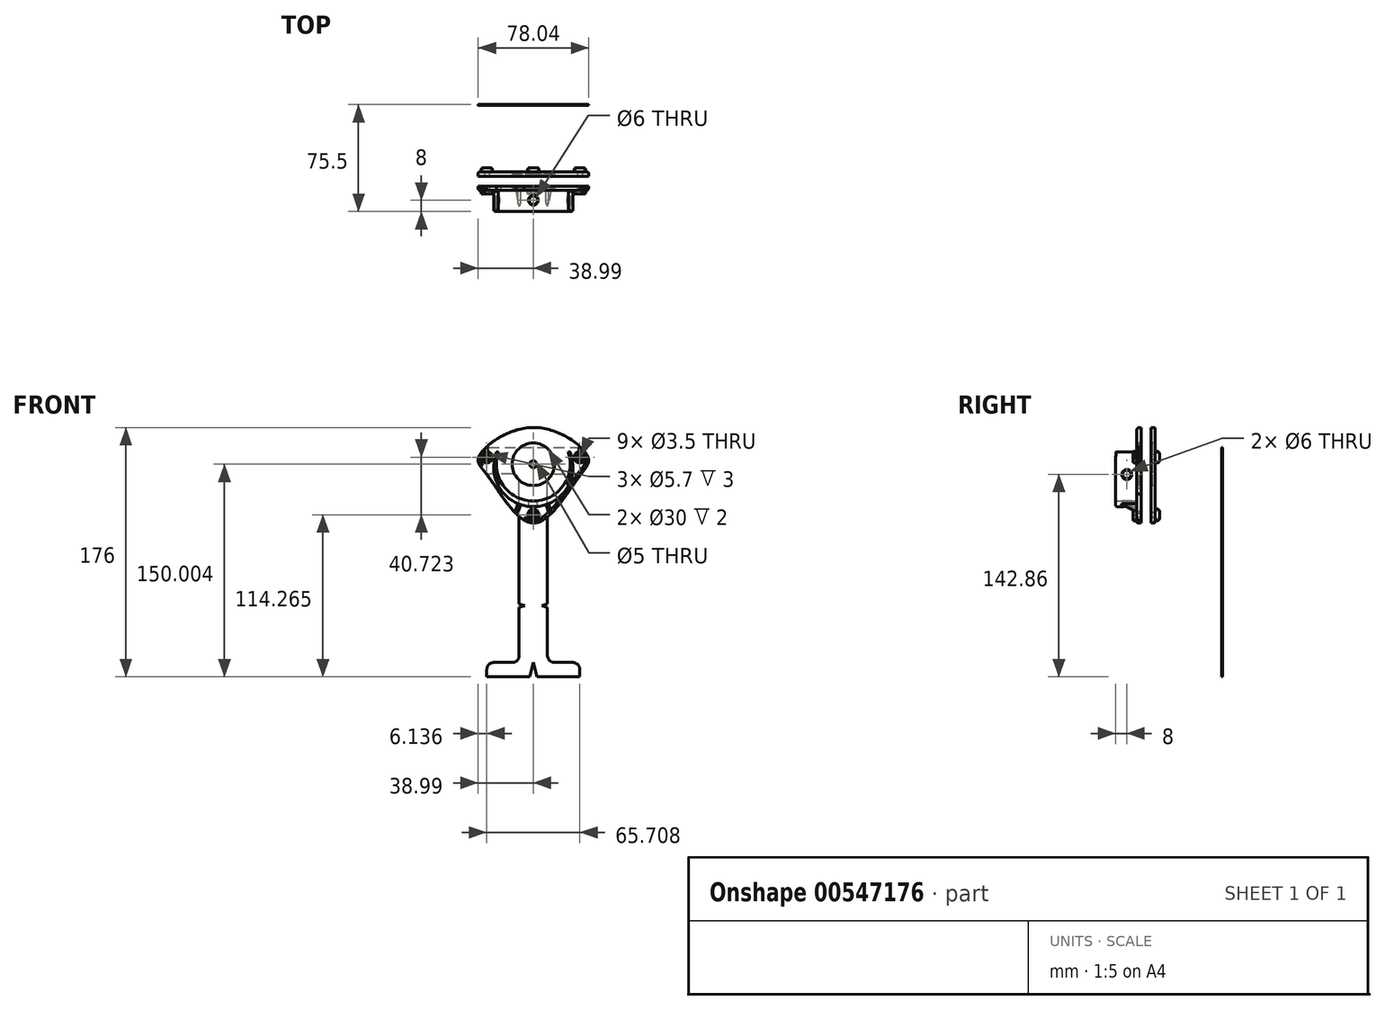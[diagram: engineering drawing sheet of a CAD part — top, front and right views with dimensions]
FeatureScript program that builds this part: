
annotation { "Feature Type Name" : "Feature", "Feature Type Description" : "" }
export const myFeature = defineFeature(function(context is Context, id is Id, definition is map)
    precondition{}
    {
        {
            var Q0;
            Q0=qCreatedBy(makeId("Front.planeOp"),FACE);
            var sketch = newSketch(context, id + "F0", { "sketchPlane" : qUnion([Q0])});
            skCircle(sketch, "E0", {"center": v(0, -2.86) * mm, "radius": 28 * mm});
            skCircle(sketch, "E1", {"center": v(0, -36.6) * mm, "radius": 1.75 * mm});
            skCircle(sketch, "E2", {"center": v(-32.85, 4.13) * mm, "radius": 1.75 * mm});
            skCircle(sketch, "E3", {"center": v(32.85, 4.13) * mm, "radius": 1.75 * mm});
            skCircle(sketch, "E4", {"center": v(0, -0.86) * mm, "radius": 26 * mm});
            skPoint(sketch, "E5", {"position": v(-38.6, 4.13) * mm});
            skPoint(sketch, "E6", {"position": v(38.6, 4.13) * mm});
            skPoint(sketch, "E7", {"position": v(0, -42.33) * mm});
            skLineSegment(sketch, "E8", {"start": v(-38.6, 4.13) * mm, "end": v(-32.85, 4.13) * mm, "construction": true});
            skLineSegment(sketch, "E9", {"start": v(-32.85, 4.13) * mm, "end": v(-27.11, 4.13) * mm, "construction": true});
            skLineSegment(sketch, "E10", {"start": v(27.11, 4.13) * mm, "end": v(32.85, 4.13) * mm, "construction": true});
            skLineSegment(sketch, "E11", {"start": v(38.6, 4.13) * mm, "end": v(32.85, 4.13) * mm, "construction": true});
            skLineSegment(sketch, "E12", {"start": v(0, -36.6) * mm, "end": v(0, -30.86) * mm, "construction": true});
            skLineSegment(sketch, "E13", {"start": v(0, -42.33) * mm, "end": v(0, -36.6) * mm, "construction": true});
            skLineSegment(sketch, "E14", {"start": v(-38.6, 0) * mm, "end": v(-38.6, 4.13) * mm, "construction": true});
            skLineSegment(sketch, "E15", {"start": v(38.6, 0) * mm, "end": v(38.6, 4.13) * mm, "construction": true});
            skPoint(sketch, "E16", {"position": v(0, 25.14) * mm});
            skFitSpline(sketch, "E17", {"points": [v(0, 25.14) * mm, v(-38.6, 4.13) * mm, v(-32.08, -9.06) * mm, v(0, -42.33) * mm, v(31.91, -10.16) * mm, v(38.6, 4.13) * mm, v(0, 25.14) * mm]});
            skLineSegment(sketch, "E18", {"start": v(-27.75, -6.56) * mm, "end": v(-32.08, -9.06) * mm, "construction": true});
            skLineSegment(sketch, "E19", {"start": v(27.58, -7.66) * mm, "end": v(31.91, -10.16) * mm, "construction": true});
            skLineSegment(sketch, "E20", {"start": v(-55.5, 8) * mm, "end": v(54.89, 8) * mm, "construction": true});
            skLineSegment(sketch, "E21", {"start": v(-25.8, 8) * mm, "end": v(-24.45, 8) * mm});
            skLineSegment(sketch, "E22", {"start": v(24.45, 8) * mm, "end": v(25.8, 8) * mm});
            skCircle(sketch, "E23", {"center": v(0, -0.86) * mm, "radius": 15 * mm});
            skCircle(sketch, "E24", {"center": v(0, -0.86) * mm, "radius": 2.5 * mm});
            skSolve(sketch);
        }
        {
            var Q0;
            Q0=makeQuery(id+"F0.imprint","IMPRINT",FACE,{"disambiguationData":[TD([[makeQuery(id+"F0.imprint","IMPRINT",EDGE,{"derivedFrom":sQuery(id+"F0.wireOp",EDGE,"E1")}),-1.0]])]});
            var Q1;
            {var subQ0=sQuery(id+"F0.wireOp",EDGE,"E21");Q1=makeQuery(id+"F0.imprint","IMPRINT",FACE,{"disambiguationData":[TD([[makeQuery(id+"F0.imprint","IMPRINT",EDGE,{"derivedFrom":subQ0}),-1.0]])]});}
            var Q2;
            {var subQ0=sQuery(id+"F0.wireOp",EDGE,"E4");var subQ4=makeQuery(id+"F0.imprint","INTERSECT",VERTEX,{"derivedFrom":[subQ0,sQuery(id+"F0.wireOp",EDGE,"E21")]});Q2=makeQuery(id+"F0.imprint","IMPRINT",FACE,{"disambiguationData":[TD([[makeQuery(id+"F0.imprint","IMPRINT",EDGE,{"disambiguationData":[TD([[subQ4,1.0]])],"derivedFrom":subQ0}),1.0]])]});}
            var Q3;
            {var subQ0=sQuery(id+"F0.wireOp",EDGE,"E21");Q3=makeQuery(id+"F0.imprint","IMPRINT",FACE,{"disambiguationData":[TD([[makeQuery(id+"F0.imprint","IMPRINT",EDGE,{"derivedFrom":subQ0}),1.0]])]});}
            var Q4;
            {var subQ0=sQuery(id+"F0.wireOp",EDGE,"E22");Q4=makeQuery(id+"F0.imprint","IMPRINT",FACE,{"disambiguationData":[TD([[makeQuery(id+"F0.imprint","IMPRINT",EDGE,{"derivedFrom":subQ0}),1.0]])]});}
            extrude(context, id + "F1", {"entities" : qUnion([Q0, Q1, Q2, Q3, Q4]), "oppositeDirection" : true, "depth" : 3 * mm, "offsetDistance" : 25 * mm});
        }
        {
            var Q0;
            Q0=makeQuery(id+"F0.imprint","IMPRINT",FACE,{"disambiguationData":[TD([[makeQuery(id+"F0.imprint","IMPRINT",EDGE,{"derivedFrom":sQuery(id+"F0.wireOp",EDGE,"E23")}),1.0]])]});
            extrude(context, id + "F2", {"entities" : qUnion([Q0]), "operationType" : NewBodyOperationType.ADD, "oppositeDirection" : true, "depth" : 3 * mm, "offsetDistance" : 25 * mm, "hasSecondDirection" : true, "secondDirectionOppositeDirection" : true, "secondDirectionDepth" : 2 * mm});
        }
        {
            var Q0;
            {var subQ0=sQuery(id+"F0.wireOp",EDGE,"E21");Q0=makeQuery(id+"F0.imprint","IMPRINT",FACE,{"disambiguationData":[TD([[makeQuery(id+"F0.imprint","IMPRINT",EDGE,{"derivedFrom":subQ0}),-1.0]])]});}
            extrude(context, id + "F3", {"entities" : qUnion([Q0]), "operationType" : NewBodyOperationType.ADD, "depth" : 15 * mm, "offsetDistance" : 25 * mm});
        }
        {
            var Q0;
            Q0=makeQuery(id+"F2.opExtrude","CAP_EDGE",EDGE,{"disambiguationData":[OSD([sQuery(id+"F0.wireOp",EDGE,"E23")])],"isStart":true});
            var Q1;
            Q1=makeQuery(id+"F2.opExtrude","CAP_EDGE",EDGE,{"disambiguationData":[OSD([sQuery(id+"F0.wireOp",EDGE,"E24")])],"isStart":true});
            fillet(context, id + "F4", {"entities" : qUnion([Q0, Q1]), "radius" : 5 * mm, "tangentPropagation" : true, "allowEdgeOverflow" : false});
        }
        {
            var Q0;
            Q0=qCreatedBy(makeId("Right.planeOp"),FACE);
            var sketch = newSketch(context, id + "F5", { "sketchPlane" : qUnion([Q0])});
            skLineSegment(sketch, "E25.bottom", {"start": v(-0.5, 11.66) * mm, "end": v(0, 11.66) * mm});
            skLineSegment(sketch, "E25.top", {"start": v(-0.5, -0.86) * mm, "end": v(0, -0.86) * mm});
            skLineSegment(sketch, "E25.left", {"start": v(-0.5, 11.66) * mm, "end": v(-0.5, -0.86) * mm});
            skLineSegment(sketch, "E25.right", {"start": v(0, 11.66) * mm, "end": v(0, -0.86) * mm});
            skSolve(sketch);
        }
        {
            var Q0;
            Q0=makeQuery(id+"F5.imprint","IMPRINT",FACE,{"disambiguationData":[TD([[makeQuery(id+"F5.imprint","IMPRINT",EDGE,{"derivedFrom":sQuery(id+"F5.wireOp",EDGE,"E25.bottom")}),-1.0]])]});
            extrude(context, id + "F6", {"entities" : qUnion([Q0]), "operationType" : NewBodyOperationType.REMOVE, "endBound" : BoundingType.SYMMETRIC, "oppositeDirection" : true, "depth" : 59.2 * mm, "offsetDistance" : 25 * mm});
        }
        {
            var Q0;
            Q0=makeQuery(id+"F6.boolean.opBoolean","MERGE",FACE,{"derivedFrom":[makeQuery(id+"F1.opExtrude","CAP_FACE",FACE,{"disambiguationData":[OSD([sQuery(id+"F0.wireOp",EDGE,"E1"),sQuery(id+"F0.wireOp",EDGE,"E2"),sQuery(id+"F0.wireOp",EDGE,"E3"),sQuery(id+"F0.wireOp",EDGE,"E17"),sQuery(id+"F0.wireOp",EDGE,"E23")])],"isStart":true}),makeQuery(id+"F6.opExtrude","SWEPT_FACE",FACE,{"disambiguationData":[OSD([sQuery(id+"F5.wireOp",EDGE,"E25.right")])]})]});
            var sketch = newSketch(context, id + "F7", { "sketchPlane" : qUnion([Q0])});
            skCircle(sketch, "E26.cCircle", {"center": v(-32.85, 4.13) * mm, "radius": 2.9 * mm, "construction": true});
            skLineSegment(sketch, "E26.0", {"start": v(-29.5, 4.13) * mm, "end": v(-31.18, 1.23) * mm});
            skLineSegment(sketch, "E26.1", {"start": v(-31.18, 1.23) * mm, "end": v(-34.53, 1.23) * mm});
            skLineSegment(sketch, "E26.2", {"start": v(-34.53, 1.23) * mm, "end": v(-36.2, 4.13) * mm});
            skLineSegment(sketch, "E26.3", {"start": v(-36.2, 4.13) * mm, "end": v(-34.53, 7.03) * mm});
            skLineSegment(sketch, "E26.4", {"start": v(-34.53, 7.03) * mm, "end": v(-31.18, 7.03) * mm});
            skLineSegment(sketch, "E26.5", {"start": v(-31.18, 7.03) * mm, "end": v(-29.5, 4.13) * mm});
            skPoint(sketch, "E26.0.midPoint", {"position": v(-30.34, 2.68) * mm});
            skCircle(sketch, "E27.cCircle", {"center": v(32.85, 4.13) * mm, "radius": 2.9 * mm, "construction": true});
            skLineSegment(sketch, "E27.0", {"start": v(29.5, 4.13) * mm, "end": v(31.18, 7.03) * mm});
            skLineSegment(sketch, "E27.1", {"start": v(31.18, 7.03) * mm, "end": v(34.53, 7.03) * mm});
            skLineSegment(sketch, "E27.2", {"start": v(34.53, 7.03) * mm, "end": v(36.2, 4.13) * mm});
            skLineSegment(sketch, "E27.3", {"start": v(36.2, 4.13) * mm, "end": v(34.53, 1.23) * mm});
            skLineSegment(sketch, "E27.4", {"start": v(34.53, 1.23) * mm, "end": v(31.18, 1.23) * mm});
            skLineSegment(sketch, "E27.5", {"start": v(31.18, 1.23) * mm, "end": v(29.5, 4.13) * mm});
            skPoint(sketch, "E27.0.midPoint", {"position": v(30.34, 5.58) * mm});
            skCircle(sketch, "E28.cCircle", {"center": v(0, -36.6) * mm, "radius": 2.9 * mm, "construction": true});
            skLineSegment(sketch, "E28.0", {"start": v(-3.35, -36.6) * mm, "end": v(-1.67, -33.7) * mm});
            skLineSegment(sketch, "E28.1", {"start": v(-1.67, -33.7) * mm, "end": v(1.67, -33.7) * mm});
            skLineSegment(sketch, "E28.2", {"start": v(1.67, -33.7) * mm, "end": v(3.35, -36.6) * mm});
            skLineSegment(sketch, "E28.3", {"start": v(3.35, -36.6) * mm, "end": v(1.67, -39.5) * mm});
            skLineSegment(sketch, "E28.4", {"start": v(1.67, -39.5) * mm, "end": v(-1.67, -39.5) * mm});
            skLineSegment(sketch, "E28.5", {"start": v(-1.67, -39.5) * mm, "end": v(-3.35, -36.6) * mm});
            skPoint(sketch, "E28.0.midPoint", {"position": v(-2.51, -35.14) * mm});
            skCircle(sketch, "E29", {"center": v(-32.85, 4.13) * mm, "radius": 4 * mm});
            skCircle(sketch, "E30", {"center": v(32.85, 4.13) * mm, "radius": 4 * mm});
            skCircle(sketch, "E31", {"center": v(0, -36.6) * mm, "radius": 4 * mm});
            skSolve(sketch);
        }
        {
            var Q0;
            Q0=makeQuery(id+"F7.imprint","IMPRINT",FACE,{"disambiguationData":[TD([[makeQuery(id+"F7.imprint","IMPRINT",EDGE,{"derivedFrom":sQuery(id+"F7.wireOp",EDGE,"E26.0")}),1.0]])]});
            var Q1;
            {var subQ0=sQuery(id+"F7.wireOp",EDGE,"E26.3");var subQ6=sQuery(id+"F7.wireOp",EDGE,"E26.4");var subQ7=makeQuery(id+"F7.imprint","INTERSECT",VERTEX,{"derivedFrom":[subQ0,subQ6]});Q1=makeQuery(id+"F7.imprint","IMPRINT",FACE,{"disambiguationData":[TD([[makeQuery(id+"F7.imprint","IMPRINT",EDGE,{"disambiguationData":[TD([[subQ7,1.0]])],"derivedFrom":subQ0}),1.0]])]});}
            var Q2;
            Q2=makeQuery(id+"F7.imprint","IMPRINT",FACE,{"disambiguationData":[TD([[makeQuery(id+"F7.imprint","IMPRINT",EDGE,{"derivedFrom":sQuery(id+"F7.wireOp",EDGE,"E27.0")}),1.0]])]});
            var Q3;
            {var subQ0=sQuery(id+"F7.wireOp",EDGE,"E30");var subQ1=sQuery(id+"F0.wireOp",EDGE,"E17");var subQ2=makeQuery(id+"F21.opFillet","BLEND_EDGE",EDGE,{"blendedFrom":[makeQuery(id+"F1.opExtrude","CAP_EDGE",EDGE,{"disambiguationData":[OSD([subQ1])],"isStart":true}),makeQuery(id+"F6.boolean.opBoolean","MERGE",FACE,{"derivedFrom":[makeQuery(id+"F1.opExtrude","CAP_FACE",FACE,{"disambiguationData":[OSD([sQuery(id+"F0.wireOp",EDGE,"E1"),sQuery(id+"F0.wireOp",EDGE,"E2"),sQuery(id+"F0.wireOp",EDGE,"E3"),subQ1,sQuery(id+"F0.wireOp",EDGE,"E23")])],"isStart":true}),makeQuery(id+"F6.opExtrude","SWEPT_FACE",FACE,{"disambiguationData":[OSD([sQuery(id+"F5.wireOp",EDGE,"E25.right")])]})]})],"blendedInto":[makeQuery(id+"F6.boolean.opBoolean","MERGE",FACE,{"derivedFrom":[makeQuery(id+"F1.opExtrude","CAP_FACE",FACE,{"disambiguationData":[OSD([sQuery(id+"F0.wireOp",EDGE,"E1"),sQuery(id+"F0.wireOp",EDGE,"E2"),sQuery(id+"F0.wireOp",EDGE,"E3"),subQ1,sQuery(id+"F0.wireOp",EDGE,"E23")])],"isStart":true}),makeQuery(id+"F6.opExtrude","SWEPT_FACE",FACE,{"disambiguationData":[OSD([sQuery(id+"F5.wireOp",EDGE,"E25.right")])]})]})]});var subQ3=makeQuery(id+"F7.imprint","INTERSECT",VERTEX,{"disambiguationData":[OD(0.0)],"derivedFrom":[subQ2,subQ0]});Q3=makeQuery(id+"F7.imprint","IMPRINT",FACE,{"disambiguationData":[TD([[makeQuery(id+"F7.imprint","IMPRINT",EDGE,{"disambiguationData":[TD([[subQ3,1.0]])],"derivedFrom":subQ0}),1.0]])]});}
            var Q4;
            Q4=makeQuery(id+"F7.imprint","IMPRINT",FACE,{"disambiguationData":[TD([[makeQuery(id+"F7.imprint","IMPRINT",EDGE,{"derivedFrom":sQuery(id+"F7.wireOp",EDGE,"E28.0")}),1.0]])]});
            extrude(context, id + "F8", {"entities" : qUnion([Q0, Q1, Q2, Q3, Q4]), "operationType" : NewBodyOperationType.ADD, "depth" : 2.5 * mm, "offsetDistance" : 25 * mm});
        }
        {
            var Q0;
            {var subQ0=sQuery(id+"F0.wireOp",EDGE,"E21");Q0=makeQuery(id+"F0.imprint","IMPRINT",FACE,{"disambiguationData":[TD([[makeQuery(id+"F0.imprint","IMPRINT",EDGE,{"derivedFrom":subQ0}),1.0]])]});}
            var Q1;
            {var subQ0=sQuery(id+"F0.wireOp",EDGE,"E21");Q1=makeQuery(id+"F0.imprint","IMPRINT",FACE,{"disambiguationData":[TD([[makeQuery(id+"F0.imprint","IMPRINT",EDGE,{"derivedFrom":subQ0}),-1.0]])]});}
            var Q2;
            {var subQ0=sQuery(id+"F0.wireOp",EDGE,"E22");Q2=makeQuery(id+"F0.imprint","IMPRINT",FACE,{"disambiguationData":[TD([[makeQuery(id+"F0.imprint","IMPRINT",EDGE,{"derivedFrom":subQ0}),1.0]])]});}
            var Q3;
            {var subQ0=sQuery(id+"F0.wireOp",EDGE,"E4");var subQ4=makeQuery(id+"F0.imprint","INTERSECT",VERTEX,{"derivedFrom":[subQ0,sQuery(id+"F0.wireOp",EDGE,"E21")]});Q3=makeQuery(id+"F0.imprint","IMPRINT",FACE,{"disambiguationData":[TD([[makeQuery(id+"F0.imprint","IMPRINT",EDGE,{"disambiguationData":[TD([[subQ4,1.0]])],"derivedFrom":subQ0}),1.0]])]});}
            var Q4;
            Q4=makeQuery(id+"F0.imprint","IMPRINT",FACE,{"disambiguationData":[TD([[makeQuery(id+"F0.imprint","IMPRINT",EDGE,{"derivedFrom":sQuery(id+"F0.wireOp",EDGE,"E1")}),-1.0]])]});
            extrude(context, id + "F9", {"entities" : qUnion([Q0, Q1, Q2, Q3, Q4]), "oppositeDirection" : true, "depth" : 13 * mm, "offsetDistance" : 25 * mm, "hasSecondDirection" : true, "secondDirectionOppositeDirection" : true, "secondDirectionDepth" : 10 * mm});
        }
        {
            var Q0;
            Q0=qCreatedBy(makeId("Right.planeOp"),FACE);
            var sketch = newSketch(context, id + "F10", { "sketchPlane" : qUnion([Q0])});
            skCircle(sketch, "E32", {"center": v(-7, -8) * mm, "radius": 3 * mm});
            skSolve(sketch);
        }
        {
            var Q0;
            Q0=makeQuery(id+"F10.imprint","IMPRINT",FACE,{"disambiguationData":[TD([[makeQuery(id+"F10.imprint","IMPRINT",EDGE,{"derivedFrom":sQuery(id+"F10.wireOp",EDGE,"E32")}),1.0]])]});
            extrude(context, id + "F11", {"entities" : qUnion([Q0]), "operationType" : NewBodyOperationType.REMOVE, "endBound" : BoundingType.SYMMETRIC, "oppositeDirection" : true, "depth" : 63 * mm, "offsetDistance" : 25 * mm});
        }
        {
            var Q0;
            {var subQ0=sQuery(id+"F0.wireOp",EDGE,"E23");var subQ2=sQuery(id+"F0.wireOp",EDGE,"E17");Q0=makeQuery(id+"F21.opFillet","SPLIT",FACE,{"disambiguationData":[OD(0.0)],"derivedFrom":makeQuery(id+"F8.boolean.opBoolean","SPLIT",FACE,{"disambiguationData":[TD([makeQuery(id+"F1.opExtrude","SWEPT_FACE",FACE,{"disambiguationData":[OSD([subQ2])]})])],"derivedFrom":makeQuery(id+"F6.boolean.opBoolean","MERGE",FACE,{"derivedFrom":[makeQuery(id+"F1.opExtrude","CAP_FACE",FACE,{"disambiguationData":[OSD([sQuery(id+"F0.wireOp",EDGE,"E1"),sQuery(id+"F0.wireOp",EDGE,"E2"),sQuery(id+"F0.wireOp",EDGE,"E3"),subQ2,subQ0])],"isStart":true}),makeQuery(id+"F6.opExtrude","SWEPT_FACE",FACE,{"disambiguationData":[OSD([sQuery(id+"F5.wireOp",EDGE,"E25.right")])]})]})})});}
            var sketch = newSketch(context, id + "F12", { "sketchPlane" : qUnion([Q0])});
            skLineSegment(sketch, "E33", {"start": v(-12.63, -33.66) * mm, "end": v(-11, -35.03) * mm});
            skLineSegment(sketch, "E34", {"start": v(-11, -35.03) * mm, "end": v(-8.26, -27.5) * mm});
            skLineSegment(sketch, "E35", {"start": v(-8.26, -27.5) * mm, "end": v(-9.9, -26.14) * mm});
            skLineSegment(sketch, "E36", {"start": v(-9.9, -26.14) * mm, "end": v(-12.63, -33.66) * mm});
            skLineSegment(sketch, "E37", {"start": v(8.26, -27.5) * mm, "end": v(9.8, -26.22) * mm});
            skLineSegment(sketch, "E38", {"start": v(9.8, -26.22) * mm, "end": v(12.53, -33.74) * mm});
            skLineSegment(sketch, "E39", {"start": v(12.53, -33.74) * mm, "end": v(11, -35.03) * mm});
            skLineSegment(sketch, "E40", {"start": v(11, -35.03) * mm, "end": v(8.26, -27.5) * mm});
            skSolve(sketch);
        }
        {
            var Q0;
            Q0 = qSketchRegion(id + "F12", true);
            extrude(context, id + "F13", {"entities" : qUnion([Q0]), "operationType" : NewBodyOperationType.ADD, "depth" : 13.5 * mm, "offsetDistance" : 25 * mm});
        }
        {
            var Q0;
            Q0=makeQuery(id+"F13.opExtrude","CAP_EDGE",EDGE,{"disambiguationData":[OSD([sQuery(id+"F12.wireOp",EDGE,"E33")])],"isStart":false});
            chamfer(context, id + "F14", {"entities" : qUnion([Q0]), "chamferType" : ChamferType.TWO_OFFSETS, "width1" : 6.5 * mm, "oppositeDirection" : false, "width2" : 13.5 * mm, "tangentPropagation" : true});
        }
        {
            var Q0;
            Q0=makeQuery(id+"F13.opExtrude","CAP_EDGE",EDGE,{"disambiguationData":[OSD([sQuery(id+"F12.wireOp",EDGE,"E39")])],"isStart":false});
            chamfer(context, id + "F15", {"entities" : qUnion([Q0]), "chamferType" : ChamferType.TWO_OFFSETS, "width1" : 6.5 * mm, "oppositeDirection" : true, "width2" : 13.5 * mm, "tangentPropagation" : true});
        }
        {
            var Q0;
            Q0=makeQuery(id+"F14.opChamfer","BLEND_EDGE",EDGE,{"blendedFrom":[makeQuery(id+"F13.opExtrude","CAP_EDGE",EDGE,{"disambiguationData":[OSD([sQuery(id+"F12.wireOp",EDGE,"E33")])],"isStart":false}),makeQuery(id+"F13.opExtrude","SWEPT_FACE",FACE,{"disambiguationData":[OSD([sQuery(id+"F12.wireOp",EDGE,"E34")])]})],"blendedInto":[makeQuery(id+"F13.opExtrude","SWEPT_FACE",FACE,{"disambiguationData":[OSD([sQuery(id+"F12.wireOp",EDGE,"E34")])]})]});
            var Q1;
            Q1=makeQuery(id+"F14.opChamfer","BLEND_EDGE",EDGE,{"blendedFrom":[makeQuery(id+"F13.opExtrude","CAP_EDGE",EDGE,{"disambiguationData":[OSD([sQuery(id+"F12.wireOp",EDGE,"E33")])],"isStart":false}),makeQuery(id+"F13.opExtrude","SWEPT_FACE",FACE,{"disambiguationData":[OSD([sQuery(id+"F12.wireOp",EDGE,"E36")])]})],"blendedInto":[makeQuery(id+"F13.opExtrude","SWEPT_FACE",FACE,{"disambiguationData":[OSD([sQuery(id+"F12.wireOp",EDGE,"E36")])]})]});
            var Q2;
            Q2=makeQuery(id+"F15.opChamfer","BLEND_EDGE",EDGE,{"blendedFrom":[makeQuery(id+"F13.opExtrude","CAP_EDGE",EDGE,{"disambiguationData":[OSD([sQuery(id+"F12.wireOp",EDGE,"E39")])],"isStart":false}),makeQuery(id+"F13.opExtrude","SWEPT_FACE",FACE,{"disambiguationData":[OSD([sQuery(id+"F12.wireOp",EDGE,"E40")])]})],"blendedInto":[makeQuery(id+"F13.opExtrude","SWEPT_FACE",FACE,{"disambiguationData":[OSD([sQuery(id+"F12.wireOp",EDGE,"E40")])]})]});
            var Q3;
            Q3=makeQuery(id+"F15.opChamfer","BLEND_EDGE",EDGE,{"blendedFrom":[makeQuery(id+"F13.opExtrude","CAP_EDGE",EDGE,{"disambiguationData":[OSD([sQuery(id+"F12.wireOp",EDGE,"E39")])],"isStart":false}),makeQuery(id+"F13.opExtrude","SWEPT_FACE",FACE,{"disambiguationData":[OSD([sQuery(id+"F12.wireOp",EDGE,"E38")])]})],"blendedInto":[makeQuery(id+"F13.opExtrude","SWEPT_FACE",FACE,{"disambiguationData":[OSD([sQuery(id+"F12.wireOp",EDGE,"E38")])]})]});
            fillet(context, id + "F16", {"entities" : qUnion([Q0, Q1, Q2, Q3]), "radius" : 1 * mm, "tangentPropagation" : true, "allowEdgeOverflow" : false});
        }
        {
            var Q0;
            Q0=qCreatedBy(makeId("Top.planeOp"),FACE);
            var sketch = newSketch(context, id + "F17", { "sketchPlane" : qUnion([Q0])});
            skCircle(sketch, "E41", {"center": v(0, -7) * mm, "radius": 3 * mm});
            skSolve(sketch);
        }
        {
            var Q0;
            Q0 = qSketchRegion(id + "F17", true);
            extrude(context, id + "F18", {"entities" : qUnion([Q0]), "operationType" : NewBodyOperationType.REMOVE, "oppositeDirection" : true, "depth" : 32 * mm, "offsetDistance" : 25 * mm, "hasSecondDirection" : true, "secondDirectionOppositeDirection" : true, "secondDirectionDepth" : 25 * mm});
        }
        {
            var Q0;
            Q0=makeQuery(id+"F11.boolean.opBoolean","COPY",FACE,{"disambiguationData":[OD(1.0)],"derivedFrom":makeQuery(id+"F11.opExtrude","SWEPT_FACE",FACE,{"disambiguationData":[OSD([sQuery(id+"F10.wireOp",EDGE,"E32")])]})});
            var Q1;
            Q1=makeQuery(id+"F11.boolean.opBoolean","COPY",FACE,{"disambiguationData":[OD(0.0)],"derivedFrom":makeQuery(id+"F11.opExtrude","SWEPT_FACE",FACE,{"disambiguationData":[OSD([sQuery(id+"F10.wireOp",EDGE,"E32")])]})});
            var Q2;
            Q2=makeQuery(id+"F18.boolean.opBoolean","COPY",FACE,{"derivedFrom":makeQuery(id+"F18.opExtrude","SWEPT_FACE",FACE,{"disambiguationData":[OSD([sQuery(id+"F17.wireOp",EDGE,"E41")])]})});
            fillet(context, id + "F19", {"entities" : qUnion([Q0, Q1, Q2]), "radius" : 0.5 * mm, "tangentPropagation" : true, "allowEdgeOverflow" : false});
        }
        {
            var Q0;
            Q0=makeQuery(id+"F8.opExtrude","CAP_EDGE",EDGE,{"disambiguationData":[OSD([sQuery(id+"F7.wireOp",EDGE,"E29")])],"isStart":true});
            var Q1;
            Q1=makeQuery(id+"F8.opExtrude","CAP_EDGE",EDGE,{"disambiguationData":[OSD([sQuery(id+"F7.wireOp",EDGE,"E31")])],"isStart":true});
            var Q2;
            Q2=makeQuery(id+"F8.opExtrude","CAP_EDGE",EDGE,{"disambiguationData":[OSD([sQuery(id+"F7.wireOp",EDGE,"E30")])],"isStart":true});
            fillet(context, id + "F20", {"entities" : qUnion([Q0, Q1, Q2]), "radius" : 2 * mm, "tangentPropagation" : true, "allowEdgeOverflow" : false});
        }
        {
            var Q0;
            Q0=makeQuery(id+"F1.opExtrude","CAP_EDGE",EDGE,{"disambiguationData":[OSD([sQuery(id+"F0.wireOp",EDGE,"E17")])],"isStart":true});
            fillet(context, id + "F21", {"entities" : qUnion([Q0]), "radius" : 2 * mm, "tangentPropagation" : true, "allowEdgeOverflow" : false});
        }
        {
            var Q0;
            Q0=makeQuery(id+"F3.opExtrude","CAP_FACE",FACE,{"disambiguationData":[OSD([sQuery(id+"F0.wireOp",EDGE,"E0"),sQuery(id+"F0.wireOp",EDGE,"E4"),sQuery(id+"F0.wireOp",EDGE,"E21"),sQuery(id+"F0.wireOp",EDGE,"E22")])],"isStart":false});
            fillet(context, id + "F22", {"entities" : qUnion([Q0]), "radius" : 1.5 * mm, "tangentPropagation" : true, "allowEdgeOverflow" : false});
        }
        {
            var Q0;
            Q0=makeQuery(id+"F3.opExtrude","SWEPT_FACE",FACE,{"disambiguationData":[OSD([sQuery(id+"F0.wireOp",EDGE,"E21")])]});
            var Q1;
            Q1=makeQuery(id+"F3.opExtrude","SWEPT_FACE",FACE,{"disambiguationData":[OSD([sQuery(id+"F0.wireOp",EDGE,"E22")])]});
            fillet(context, id + "F23", {"entities" : qUnion([Q0, Q1]), "radius" : 0.65 * mm, "tangentPropagation" : true, "allowEdgeOverflow" : false});
        }
        {
            var Q0;
            Q0=makeQuery(id+"F0.imprint","IMPRINT",FACE,{"disambiguationData":[TD([[makeQuery(id+"F0.imprint","IMPRINT",EDGE,{"derivedFrom":sQuery(id+"F0.wireOp",EDGE,"E23")}),1.0]])]});
            extrude(context, id + "F24", {"entities" : qUnion([Q0]), "operationType" : NewBodyOperationType.ADD, "oppositeDirection" : true, "depth" : 11 * mm, "offsetDistance" : 25 * mm, "hasSecondDirection" : true, "secondDirectionOppositeDirection" : true, "secondDirectionDepth" : 10 * mm});
        }
        {
            var Q0;
            Q0=makeQuery(id+"F24.opExtrude","CAP_EDGE",EDGE,{"disambiguationData":[OSD([sQuery(id+"F0.wireOp",EDGE,"E23")])],"isStart":false});
            var Q1;
            Q1=makeQuery(id+"F24.opExtrude","CAP_EDGE",EDGE,{"disambiguationData":[OSD([sQuery(id+"F0.wireOp",EDGE,"E24")])],"isStart":false});
            fillet(context, id + "F25", {"entities" : qUnion([Q0, Q1]), "radius" : 6 * mm, "tangentPropagation" : true, "allowEdgeOverflow" : false});
        }
        {
            var Q0;
            Q0=makeQuery(id+"F9.opExtrude","CAP_FACE",FACE,{"disambiguationData":[OSD([sQuery(id+"F0.wireOp",EDGE,"E1"),sQuery(id+"F0.wireOp",EDGE,"E2"),sQuery(id+"F0.wireOp",EDGE,"E3"),sQuery(id+"F0.wireOp",EDGE,"E17"),sQuery(id+"F0.wireOp",EDGE,"E23")])],"isStart":false});
            var sketch = newSketch(context, id + "F26", { "sketchPlane" : qUnion([Q0])});
            skCircle(sketch, "E42", {"center": v(-32.85, 4.13) * mm, "radius": 2.85 * mm});
            skCircle(sketch, "E43", {"center": v(0, -36.6) * mm, "radius": 2.85 * mm});
            skCircle(sketch, "E44", {"center": v(32.85, 4.13) * mm, "radius": 2.85 * mm});
            skCircle(sketch, "E45", {"center": v(-32.85, 4.13) * mm, "radius": 4 * mm});
            skCircle(sketch, "E46", {"center": v(0, -36.6) * mm, "radius": 4 * mm});
            skCircle(sketch, "E47", {"center": v(32.85, 4.13) * mm, "radius": 4 * mm});
            skSolve(sketch);
        }
        {
            var Q0;
            Q0 = qSketchRegion(id + "F26", true);
            extrude(context, id + "F27", {"entities" : qUnion([Q0]), "operationType" : NewBodyOperationType.ADD, "depth" : 3 * mm, "offsetDistance" : 25 * mm});
        }
        {
            var Q0;
            Q0=makeQuery(id+"F27.opExtrude","CAP_EDGE",EDGE,{"disambiguationData":[OSD([sQuery(id+"F26.wireOp",EDGE,"E45")])],"isStart":true});
            var Q1;
            Q1=makeQuery(id+"F27.opExtrude","CAP_EDGE",EDGE,{"disambiguationData":[OSD([sQuery(id+"F26.wireOp",EDGE,"E47")])],"isStart":true});
            var Q2;
            Q2=makeQuery(id+"F27.opExtrude","CAP_EDGE",EDGE,{"disambiguationData":[OSD([sQuery(id+"F26.wireOp",EDGE,"E46")])],"isStart":true});
            var Q3;
            Q3=makeQuery(id+"F27.opExtrude","CAP_EDGE",EDGE,{"disambiguationData":[OSD([sQuery(id+"F26.wireOp",EDGE,"E45")])],"isStart":false});
            var Q4;
            Q4=makeQuery(id+"F27.opExtrude","CAP_EDGE",EDGE,{"disambiguationData":[OSD([sQuery(id+"F26.wireOp",EDGE,"E47")])],"isStart":false});
            var Q5;
            Q5=makeQuery(id+"F27.opExtrude","SWEPT_FACE",FACE,{"disambiguationData":[OSD([sQuery(id+"F26.wireOp",EDGE,"E46")])]});
            fillet(context, id + "F28", {"entities" : qUnion([Q0, Q1, Q2, Q3, Q4, Q5]), "radius" : 1.5 * mm, "tangentPropagation" : true, "allowEdgeOverflow" : false});
        }
        {
            var Q0;
            Q0=makeQuery(id+"F9.opExtrude","CAP_EDGE",EDGE,{"disambiguationData":[OSD([sQuery(id+"F0.wireOp",EDGE,"E17")])],"isStart":false});
            fillet(context, id + "F29", {"entities" : qUnion([Q0]), "radius" : 1 * mm, "tangentPropagation" : true, "allowEdgeOverflow" : false});
        }
        {
            var Q0;
            Q0=makeQuery(id+"F0.imprint","IMPRINT",FACE,{"disambiguationData":[TD([[makeQuery(id+"F0.imprint","IMPRINT",EDGE,{"derivedFrom":sQuery(id+"F0.wireOp",EDGE,"E23")}),1.0]])]});
            var Q1;
            Q1=makeQuery(id+"F0.imprint","IMPRINT",FACE,{"disambiguationData":[TD([[makeQuery(id+"F0.imprint","IMPRINT",EDGE,{"derivedFrom":sQuery(id+"F0.wireOp",EDGE,"E23")}),-1.0]])]});
            var Q2;
            {var subQ0=sQuery(id+"F0.wireOp",EDGE,"E21");Q2=makeQuery(id+"F0.imprint","IMPRINT",FACE,{"disambiguationData":[TD([[makeQuery(id+"F0.imprint","IMPRINT",EDGE,{"derivedFrom":subQ0}),-1.0]])]});}
            var Q3;
            Q3=makeQuery(id+"F0.imprint","IMPRINT",FACE,{"disambiguationData":[TD([[makeQuery(id+"F0.imprint","IMPRINT",EDGE,{"derivedFrom":sQuery(id+"F0.wireOp",EDGE,"E1")}),-1.0]])]});
            var Q4;
            {var subQ0=sQuery(id+"F0.wireOp",EDGE,"E22");Q4=makeQuery(id+"F0.imprint","IMPRINT",FACE,{"disambiguationData":[TD([[makeQuery(id+"F0.imprint","IMPRINT",EDGE,{"derivedFrom":subQ0}),1.0]])]});}
            var Q5;
            {var subQ0=sQuery(id+"F0.wireOp",EDGE,"E21");Q5=makeQuery(id+"F0.imprint","IMPRINT",FACE,{"disambiguationData":[TD([[makeQuery(id+"F0.imprint","IMPRINT",EDGE,{"derivedFrom":subQ0}),1.0]])]});}
            extrude(context, id + "F30", {"entities" : qUnion([Q0, Q1, Q2, Q3, Q4, Q5]), "oppositeDirection" : true, "depth" : 60.5 * mm, "offsetDistance" : 25 * mm, "hasSecondDirection" : true, "secondDirectionOppositeDirection" : true, "secondDirectionDepth" : 60 * mm});
        }
        {
            var Q0;
            Q0=makeQuery(id+"F30.opExtrude","CAP_FACE",FACE,{"disambiguationData":[OSD([sQuery(id+"F0.wireOp",EDGE,"E1"),sQuery(id+"F0.wireOp",EDGE,"E2"),sQuery(id+"F0.wireOp",EDGE,"E3"),sQuery(id+"F0.wireOp",EDGE,"E17"),sQuery(id+"F0.wireOp",EDGE,"E24")])],"isStart":true});
            var sketch = newSketch(context, id + "F31", { "sketchPlane" : qUnion([Q0])});
            skLineSegment(sketch, "E48.bottom", {"start": v(-32.85, 11.64) * mm, "end": v(32.85, 11.64) * mm});
            skLineSegment(sketch, "E48.top", {"start": v(-32.85, -150.86) * mm, "end": v(32.85, -150.86) * mm});
            skLineSegment(sketch, "E48.left", {"start": v(-32.85, 11.64) * mm, "end": v(-32.85, -150.86) * mm});
            skLineSegment(sketch, "E48.right", {"start": v(32.85, 11.64) * mm, "end": v(32.85, -150.86) * mm});
            skCircle(sketch, "E49", {"center": v(0, -0.86) * mm, "radius": 4.65 * mm});
            skLineSegment(sketch, "E50", {"start": v(0, -150.86) * mm, "end": v(0, -140.86) * mm, "construction": true});
            skLineSegment(sketch, "E51", {"start": v(0, -140.86) * mm, "end": v(-2.5, -150.86) * mm});
            skLineSegment(sketch, "E52", {"start": v(0, -140.86) * mm, "end": v(2.5, -150.86) * mm});
            skSolve(sketch);
        }
        {
            var Q0;
            {var subQ0=sQuery(id+"F31.wireOp",EDGE,"E48.top");Q0=makeQuery(id+"F31.imprint","IMPRINT",FACE,{"disambiguationData":[TD([[makeQuery(id+"F31.imprint","IMPRINT",EDGE,{"derivedFrom":subQ0}),1.0]])]});}
            extrude(context, id + "F32", {"entities" : qUnion([Q0]), "operationType" : NewBodyOperationType.ADD, "oppositeDirection" : true, "depth" : 0.5 * mm, "offsetDistance" : 25 * mm});
        }
        {
            var Q0;
            {var subQ0=sQuery(id+"F0.wireOp",EDGE,"E17");Q0=makeQuery(id+"F32.boolean.opBoolean","MERGE",FACE,{"derivedFrom":[makeQuery(id+"F30.opExtrude","CAP_FACE",FACE,{"disambiguationData":[OSD([sQuery(id+"F0.wireOp",EDGE,"E1"),sQuery(id+"F0.wireOp",EDGE,"E2"),sQuery(id+"F0.wireOp",EDGE,"E3"),subQ0,sQuery(id+"F0.wireOp",EDGE,"E24")])],"isStart":false}),makeQuery(id+"F32.opExtrude","CAP_FACE",FACE,{"disambiguationData":[OSD([subQ0,sQuery(id+"F31.wireOp",EDGE,"E48.top"),sQuery(id+"F31.wireOp",EDGE,"E48.left"),sQuery(id+"F31.wireOp",EDGE,"E48.right"),sQuery(id+"F31.wireOp",EDGE,"E51"),sQuery(id+"F31.wireOp",EDGE,"E52")])],"isStart":false})]});}
            var sketch = newSketch(context, id + "F33", { "sketchPlane" : qUnion([Q0])});
            skLineSegment(sketch, "E53.bottom", {"start": v(-43.57, -7.62) * mm, "end": v(-15, -7.62) * mm});
            skLineSegment(sketch, "E53.top", {"start": v(-43.57, -140.86) * mm, "end": v(-15, -140.86) * mm});
            skLineSegment(sketch, "E53.left", {"start": v(-43.57, -7.62) * mm, "end": v(-43.57, -140.86) * mm});
            skLineSegment(sketch, "E53.right", {"start": v(-10, -12.62) * mm, "end": v(-10, -135.86) * mm});
            skLineSegment(sketch, "E54.bottom", {"start": v(43.13, -7.62) * mm, "end": v(15, -7.62) * mm});
            skLineSegment(sketch, "E54.top", {"start": v(43.13, -140.86) * mm, "end": v(15, -140.86) * mm});
            skLineSegment(sketch, "E54.left", {"start": v(43.13, -7.62) * mm, "end": v(43.13, -140.86) * mm});
            skLineSegment(sketch, "E54.right", {"start": v(10, -12.62) * mm, "end": v(10, -135.86) * mm});
            skLineSegment(sketch, "E55.bottom", {"start": v(-59.63, 39.02) * mm, "end": v(64.86, 39.02) * mm});
            skLineSegment(sketch, "E55.top", {"start": v(-59.63, 10.88) * mm, "end": v(64.86, 10.88) * mm});
            skLineSegment(sketch, "E55.left", {"start": v(-59.63, 39.02) * mm, "end": v(-59.63, 10.88) * mm});
            skLineSegment(sketch, "E55.right", {"start": v(64.86, 39.02) * mm, "end": v(64.86, 10.88) * mm});
            skPoint(sketch, "E56.visualSharp", {"position": v(-10, -7.62) * mm});
            skArc(sketch, "E56.filletArc", {"start": v(-10, -12.62) * mm, "mid": v(-11.46, -9.09) * mm, "end": v(-15, -7.62) * mm});
            skPoint(sketch, "E57.visualSharp", {"position": v(10, -7.62) * mm});
            skArc(sketch, "E57.filletArc", {"start": v(15, -7.62) * mm, "mid": v(11.46, -9.09) * mm, "end": v(10, -12.62) * mm});
            skPoint(sketch, "E58.visualSharp", {"position": v(10, -140.86) * mm});
            skArc(sketch, "E58.filletArc", {"start": v(10, -135.86) * mm, "mid": v(11.46, -139.4) * mm, "end": v(15, -140.86) * mm});
            skPoint(sketch, "E59.visualSharp", {"position": v(-10, -140.86) * mm});
            skArc(sketch, "E59.filletArc", {"start": v(-15, -140.86) * mm, "mid": v(-11.46, -139.4) * mm, "end": v(-10, -135.86) * mm});
            skLineSegment(sketch, "E60", {"start": v(-10, -100.86) * mm, "end": v(10, -100.86) * mm, "construction": true});
            skLineSegment(sketch, "E61", {"start": v(10, -99.6) * mm, "end": v(6, -100.86) * mm});
            skLineSegment(sketch, "E62", {"start": v(6, -100.86) * mm, "end": v(10, -102.1) * mm});
            skLineSegment(sketch, "E63", {"start": v(-10, -102.1) * mm, "end": v(-6, -100.86) * mm});
            skLineSegment(sketch, "E64", {"start": v(-6, -100.86) * mm, "end": v(-10, -99.6) * mm});
            skSolve(sketch);
        }
        {
            var Q0;
            Q0 = qSketchRegion(id + "F33", true);
            extrude(context, id + "F34", {"entities" : qUnion([Q0]), "operationType" : NewBodyOperationType.REMOVE, "endBound" : BoundingType.SYMMETRIC, "oppositeDirection" : true, "depth" : 25 * mm, "offsetDistance" : 25 * mm});
        }
        {
            var Q0;
            Q0=makeQuery(id+"F34.boolean.opBoolean","INTERSECT",EDGE,{"disambiguationData":[OD(1.0)],"derivedFrom":[makeQuery(id+"F30.opExtrude","SWEPT_FACE",FACE,{"disambiguationData":[OSD([sQuery(id+"F0.wireOp",EDGE,"E17")])]}),makeQuery(id+"F34.opExtrude","SWEPT_FACE",FACE,{"disambiguationData":[OSD([sQuery(id+"F33.wireOp",EDGE,"E55.top")])]})]});
            var Q1;
            Q1=makeQuery(id+"F34.boolean.opBoolean","INTERSECT",EDGE,{"disambiguationData":[OD(0.0)],"derivedFrom":[makeQuery(id+"F30.opExtrude","SWEPT_FACE",FACE,{"disambiguationData":[OSD([sQuery(id+"F0.wireOp",EDGE,"E17")])]}),makeQuery(id+"F34.opExtrude","SWEPT_FACE",FACE,{"disambiguationData":[OSD([sQuery(id+"F33.wireOp",EDGE,"E55.top")])]})]});
            var Q2;
            Q2=makeQuery(id+"F34.boolean.opBoolean","INTERSECT",EDGE,{"derivedFrom":[makeQuery(id+"F30.opExtrude","SWEPT_FACE",FACE,{"disambiguationData":[OSD([sQuery(id+"F0.wireOp",EDGE,"E17")])]}),makeQuery(id+"F34.opExtrude","SWEPT_FACE",FACE,{"disambiguationData":[OSD([sQuery(id+"F33.wireOp",EDGE,"E53.bottom")])]})]});
            var Q3;
            Q3=makeQuery(id+"F34.boolean.opBoolean","INTERSECT",EDGE,{"derivedFrom":[makeQuery(id+"F30.opExtrude","SWEPT_FACE",FACE,{"disambiguationData":[OSD([sQuery(id+"F0.wireOp",EDGE,"E17")])]}),makeQuery(id+"F34.opExtrude","SWEPT_FACE",FACE,{"disambiguationData":[OSD([sQuery(id+"F33.wireOp",EDGE,"E54.bottom")])]})]});
            var Q4;
            Q4=makeQuery(id+"F34.boolean.opBoolean","INTERSECT",EDGE,{"derivedFrom":[makeQuery(id+"F32.opExtrude","SWEPT_FACE",FACE,{"disambiguationData":[OSD([sQuery(id+"F31.wireOp",EDGE,"E48.right")])]}),makeQuery(id+"F34.opExtrude","SWEPT_FACE",FACE,{"disambiguationData":[OSD([sQuery(id+"F33.wireOp",EDGE,"E53.top")])]})]});
            var Q5;
            Q5=makeQuery(id+"F34.boolean.opBoolean","INTERSECT",EDGE,{"derivedFrom":[makeQuery(id+"F32.opExtrude","SWEPT_FACE",FACE,{"disambiguationData":[OSD([sQuery(id+"F31.wireOp",EDGE,"E48.left")])]}),makeQuery(id+"F34.opExtrude","SWEPT_FACE",FACE,{"disambiguationData":[OSD([sQuery(id+"F33.wireOp",EDGE,"E54.top")])]})]});
            fillet(context, id + "F35", {"entities" : qUnion([Q0, Q1, Q2, Q3, Q4, Q5]), "radius" : 5 * mm, "tangentPropagation" : true, "allowEdgeOverflow" : false});
        }
    });
